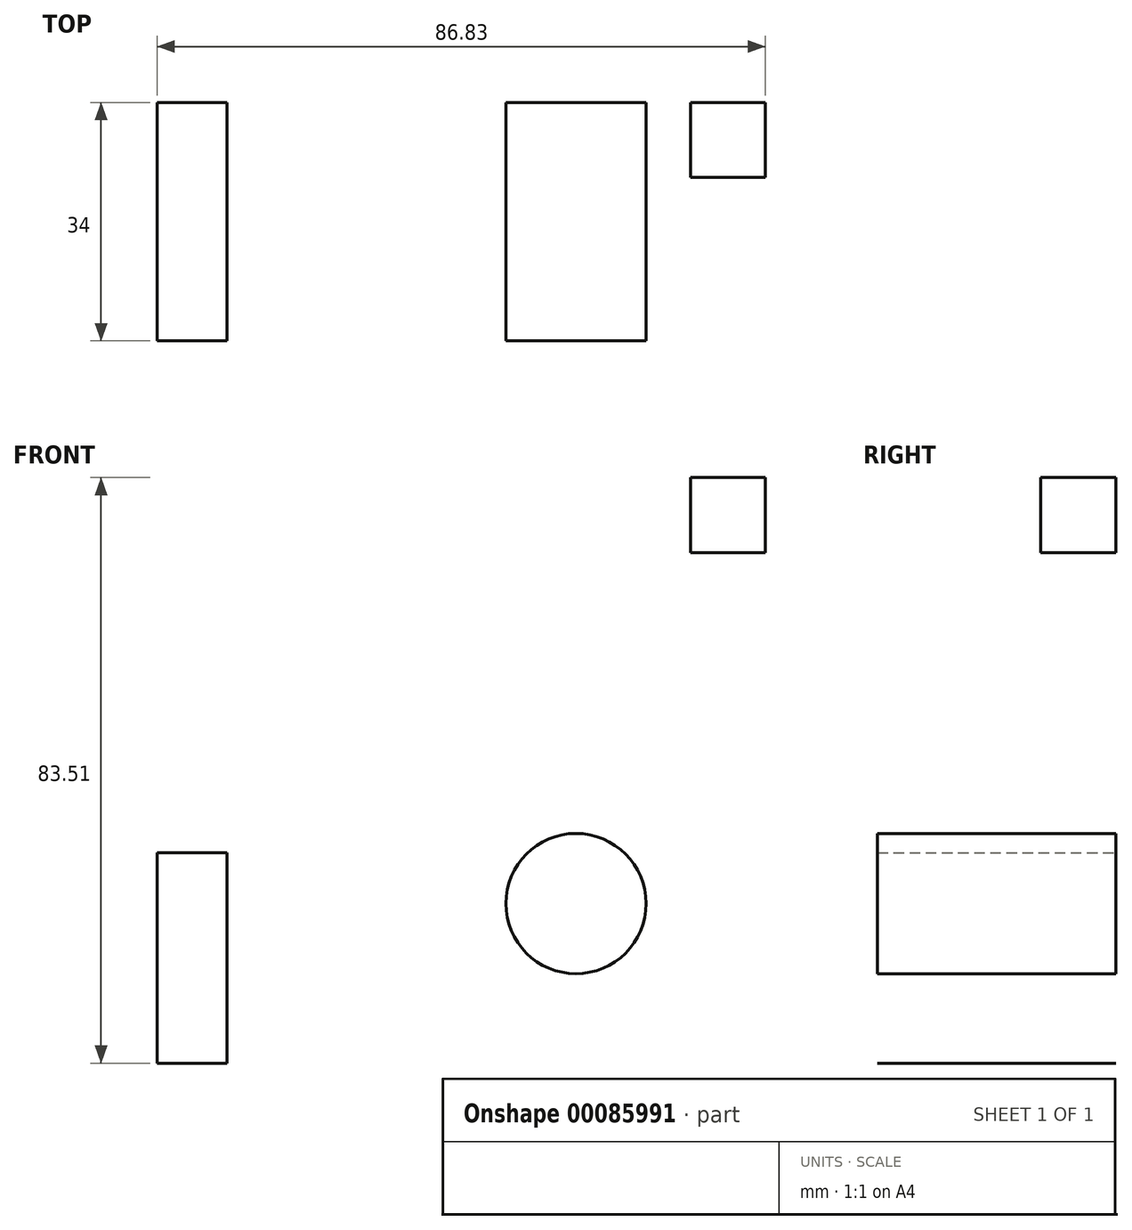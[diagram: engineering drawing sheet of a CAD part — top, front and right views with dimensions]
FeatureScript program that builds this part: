
annotation { "Feature Type Name" : "Feature", "Feature Type Description" : "" }
export const myFeature = defineFeature(function(context is Context, id is Id, definition is map)
    precondition{}
    {
        {
            var Q0;
            Q0=qCreatedBy(makeId("Front.planeOp"),FACE);
            var sketch = newSketch(context, id + "F0", { "sketchPlane" : qUnion([Q0])});
            skCircle(sketch, "E0", {"center": v(0, 0) * mm, "radius": 10 * mm});
            skLineSegment(sketch, "E1.bottom", {"start": v(-59.8, 7.24) * mm, "end": v(-49.8, 7.24) * mm});
            skLineSegment(sketch, "E1.top", {"start": v(-59.8, -22.76) * mm, "end": v(-49.8, -22.76) * mm});
            skLineSegment(sketch, "E1.left", {"start": v(-59.8, 7.24) * mm, "end": v(-59.8, -22.76) * mm});
            skLineSegment(sketch, "E1.right", {"start": v(-49.8, 7.24) * mm, "end": v(-49.8, -22.76) * mm});
            skSolve(sketch);
        }
        {
            var Q0;
            Q0=makeQuery(id+"F0.imprint","IMPRINT",FACE,{"disambiguationData":[TD([[makeQuery(id+"F0.imprint","IMPRINT",EDGE,{"derivedFrom":sQuery(id+"F0.wireOp",EDGE,"E0")}),1.0]])]});
            var Q1;
            Q1=makeQuery(id+"F0.imprint","IMPRINT",FACE,{"disambiguationData":[TD([[makeQuery(id+"F0.imprint","IMPRINT",EDGE,{"derivedFrom":sQuery(id+"F0.wireOp",EDGE,"E1.bottom")}),-1.0]])]});
            extrude(context, id + "F1", {"entities" : qUnion([Q0, Q1]), "depth" : 34 * mm});
        }
        {
            var Q0;
            Q0=qCreatedBy(makeId("Front.planeOp"),FACE);
            var sketch = newSketch(context, id + "F2", { "sketchPlane" : qUnion([Q0])});
            skLineSegment(sketch, "E2.bottom", {"start": v(16.34, 60.75) * mm, "end": v(27.04, 60.75) * mm});
            skLineSegment(sketch, "E2.top", {"start": v(16.34, 50.05) * mm, "end": v(27.04, 50.05) * mm});
            skLineSegment(sketch, "E2.left", {"start": v(16.34, 60.75) * mm, "end": v(16.34, 50.05) * mm});
            skLineSegment(sketch, "E2.right", {"start": v(27.04, 60.75) * mm, "end": v(27.04, 50.05) * mm});
            skSolve(sketch);
        }
        {
            var Q0;
            Q0=makeQuery(id+"F2.imprint","IMPRINT",FACE,{"disambiguationData":[TD([[makeQuery(id+"F2.imprint","IMPRINT",EDGE,{"derivedFrom":sQuery(id+"F2.wireOp",EDGE,"E2.bottom")}),-1.0]])]});
            extrude(context, id + "F3", {"entities" : qUnion([Q0]), "depth" : 10.7 * mm});
        }
    });
